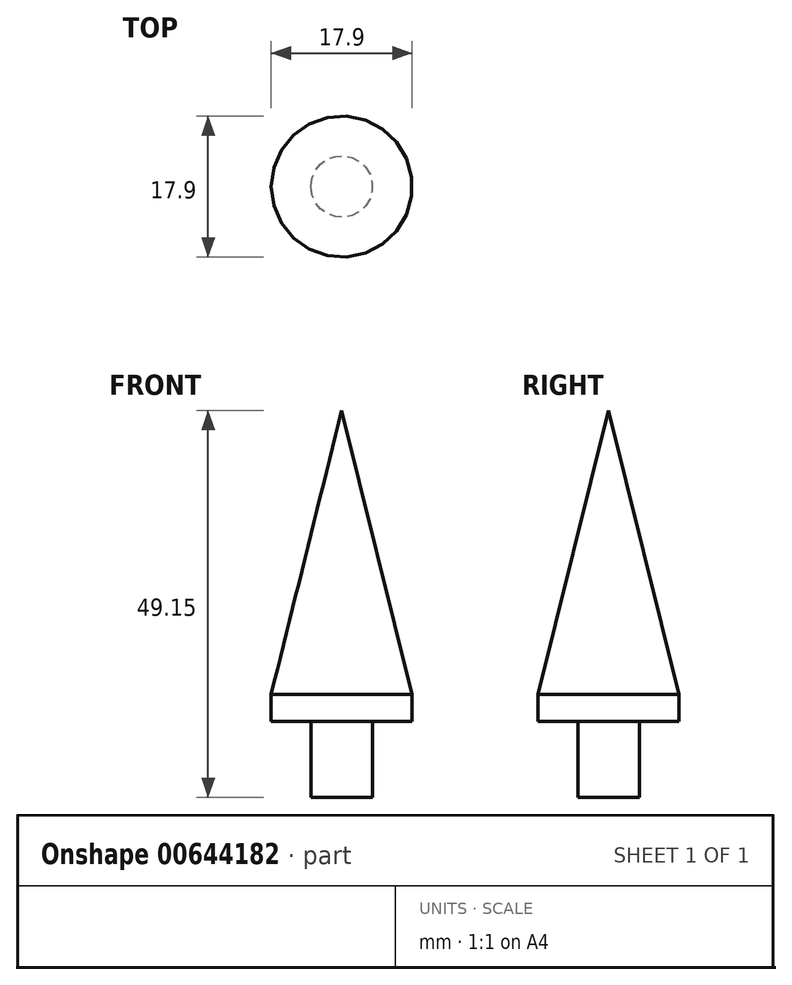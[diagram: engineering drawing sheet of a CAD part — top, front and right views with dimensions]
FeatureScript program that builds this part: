
annotation { "Feature Type Name" : "Feature", "Feature Type Description" : "" }
export const myFeature = defineFeature(function(context is Context, id is Id, definition is map)
    precondition{}
    {
        {
            var Q0;
            Q0=qCreatedBy(makeId("Front.planeOp"),FACE);
            var sketch = newSketch(context, id + "F0", { "sketchPlane" : qUnion([Q0])});
            skLineSegment(sketch, "E0.top", {"start": v(16.57, -20.04) * mm, "end": v(20.48, -20.04) * mm});
            skLineSegment(sketch, "E0.right", {"start": v(20.48, -10.37) * mm, "end": v(20.48, -20.04) * mm});
            skLineSegment(sketch, "E1", {"start": v(20.48, -10.37) * mm, "end": v(25.52, -10.37) * mm});
            skLineSegment(sketch, "E2", {"start": v(16.57, -20.04) * mm, "end": v(16.57, 29.11) * mm});
            skLineSegment(sketch, "E3", {"start": v(25.52, -10.37) * mm, "end": v(25.52, -6.94) * mm});
            skLineSegment(sketch, "E4", {"start": v(25.52, -6.94) * mm, "end": v(16.57, 29.11) * mm});
            skSolve(sketch);
        }
        {
            var Q0;
            Q0=makeQuery(id+"F0.imprint","IMPRINT",FACE,{"disambiguationData":[TD([[makeQuery(id+"F0.imprint","IMPRINT",EDGE,{"derivedFrom":sQuery(id+"F0.wireOp",EDGE,"E0.top")}),1.0]])]});
            var Q1;
            Q1=sQuery(id+"F0.wireOp",EDGE,"E2");
            revolve(context, id + "F1", {"entities" : qUnion([Q0]), "axis" : qUnion([Q1]), "revolveType" : RevolveType.FULL});
        }
    });
